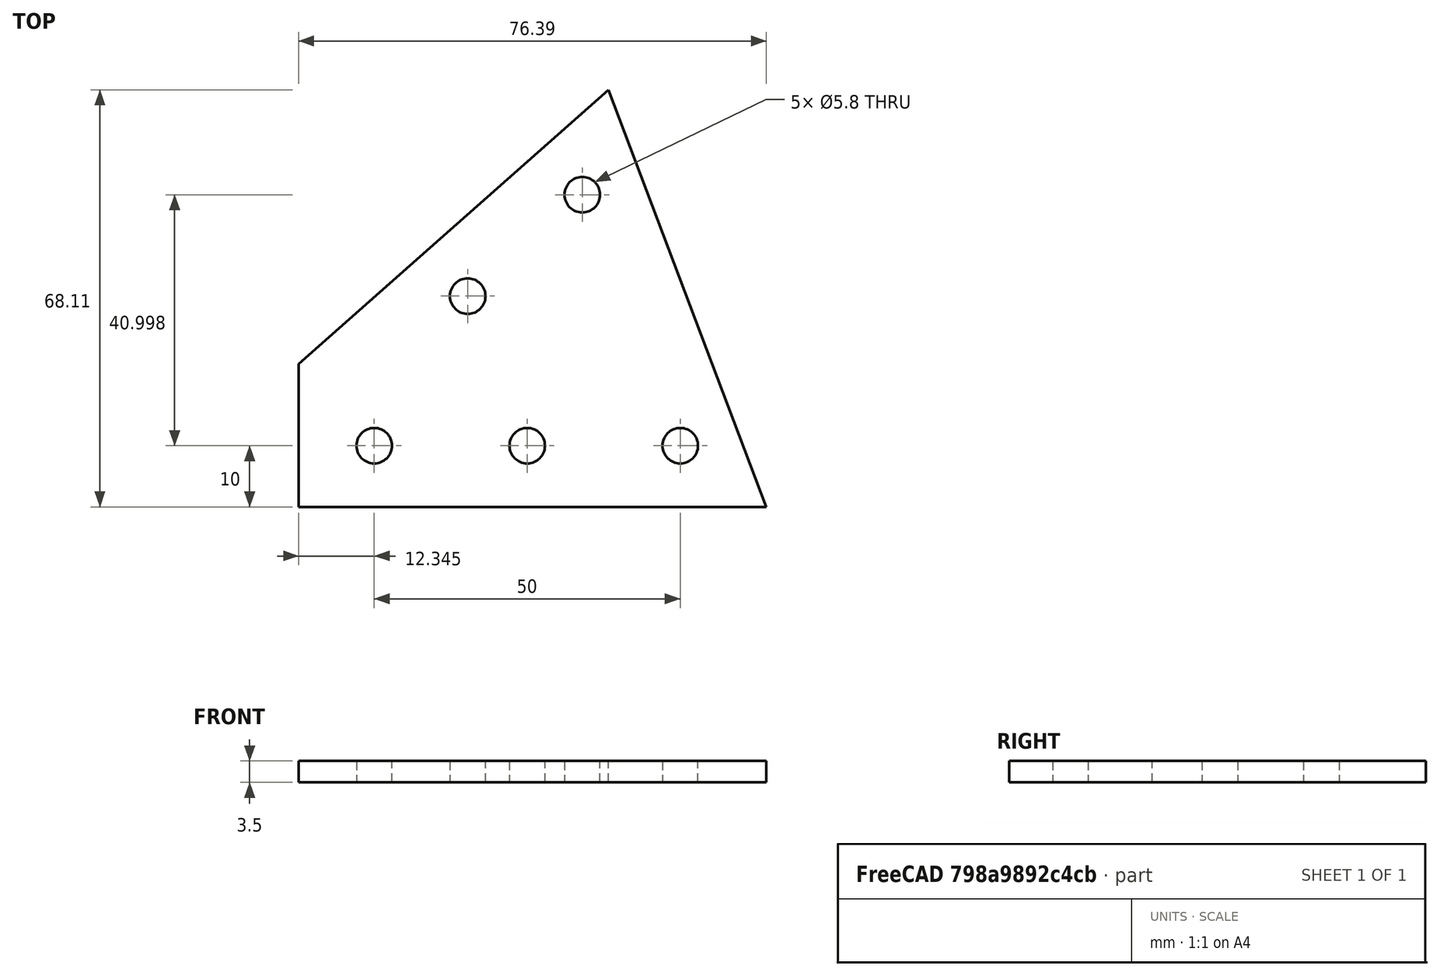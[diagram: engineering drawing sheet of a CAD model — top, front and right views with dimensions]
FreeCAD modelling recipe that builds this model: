
FCSTD DOCUMENT  (FreeCAD 0.16R6607 (Git))
Label: frame_corner_41.5_degree
License: CreativeCommons Attribution-ShareAlike
LicenseURL: http://creativecommons.org/licenses/by-sa/4.0/
objects: Sketcher::SketchObject×1, PartDesign::Pad×1
note: 3 computed .brp shape members not serialized (recipe doc carries the construction recipe); baked Part::Feature solids carry a one-line shape summary decoded from their .brp

FEATURE [Sketcher::SketchObject] Sketch
  sketch-geometry (21):
    g0: LineSegment [constr] StartX=57.2161 StartY=50.6206 StartZ=0 EndX=0 EndY=0 EndZ=0
    g1: LineSegment [constr] StartX=0 StartY=0 StartZ=0 EndX=76.3945 EndY=0 EndZ=0
    g2: LineSegment [constr] StartX=0 StartY=10 StartZ=0 EndX=76.3945 EndY=10 EndZ=0
    g3: LineSegment [constr] StartX=76.3945 StartY=10 StartZ=0 EndX=76.3945 EndY=-10 EndZ=0
    g4: LineSegment [constr] StartX=76.3945 StartY=-10 StartZ=0 EndX=0 EndY=-10 EndZ=0
    g5: LineSegment [constr] StartX=0 StartY=-10 StartZ=0 EndX=0 EndY=10 EndZ=0
    g6: LineSegment [constr] StartX=13.1421 StartY=24.9791 StartZ=0 EndX=50.5899 EndY=58.1101 EndZ=0
    g7: LineSegment [constr] StartX=50.5899 StartY=58.1101 StartZ=0 EndX=63.8423 EndY=43.131 EndZ=0
    g8: LineSegment [constr] StartX=63.8423 StartY=43.131 StartZ=0 EndX=26.3945 EndY=10 EndZ=0
    g9: LineSegment [constr] StartX=26.3945 StartY=10 StartZ=0 EndX=13.1421 EndY=24.9791 EndZ=0
    g10: LineSegment [constr] StartX=13.1421 StartY=24.9791 StartZ=0 EndX=-26.3945 EndY=-10 EndZ=0
    g11: LineSegment [constr] StartX=-26.3945 StartY=-10 StartZ=0 EndX=0 EndY=-10 EndZ=0
    g12: LineSegment StartX=0 StartY=-10 StartZ=0 EndX=0 EndY=13.3519 EndZ=0
    g13: LineSegment StartX=0 StartY=13.3519 StartZ=0 EndX=50.5899 EndY=58.1101 EndZ=0
    g14: LineSegment StartX=50.5899 StartY=58.1101 StartZ=0 EndX=76.3945 EndY=-10 EndZ=0
    g15: LineSegment StartX=76.3945 StartY=-10 StartZ=0 EndX=0 EndY=-10 EndZ=0
    g16: Circle CenterX=27.6164 CenterY=24.4329 CenterZ=0 NormalX=0 NormalY=0 NormalZ=1 Radius=2.9
    g17: Circle CenterX=46.3403 CenterY=40.9984 CenterZ=0 NormalX=0 NormalY=0 NormalZ=1 Radius=2.9
    g18: Circle CenterX=62.3447 CenterY=0 CenterZ=0 NormalX=0 NormalY=0 NormalZ=1 Radius=2.9
    g19: Circle CenterX=37.3447 CenterY=0 CenterZ=0 NormalX=0 NormalY=0 NormalZ=1 Radius=2.9
    g20: Circle CenterX=12.3447 CenterY=0 CenterZ=0 NormalX=0 NormalY=0 NormalZ=1 Radius=2.9
  constraints (58):
    c: Coincident(g0,g1)
    c: Angle(g1,g0) = 0.724312
    c: Horizontal(g1)
    c: Equal(g0,g1)
    c: Coincident(g0,g-1)
    c: Coincident(g2,g3)
    c: Coincident(g3,g4)
    c: Coincident(g4,g5)
    c: Coincident(g5,g2)
    c: Horizontal(g2)
    c: Horizontal(g4)
    c: Vertical(g3)
    c: Vertical(g5)
    c: Coincident(g6,g7)
    c: Coincident(g7,g8)
    c: Coincident(g8,g9)
    c: Coincident(g9,g6)
    c: Parallel(g6,g8)
    c: Parallel(g8,g0)
    c: Perpendicular(g8,g9)
    c: Perpendicular(g8,g7)
    c: Distance(g9) = 20
    c: DistanceY(g5) = 20
    c: PointOnObject(g0,g7)
    c: Distance(g7,g0) = 10
    c: PointOnObject(g8,g2)
    c: DistanceY(g1,g3) = -10
    c: PointOnObject(g-1,g5)
    c: PointOnObject(g1,g3)
    c: Distance(g6,g6) = 50
    c: Coincident(g10,g11)
    c: Coincident(g4,g11)
    c: Coincident(g6,g10)
    c: Angle(g11,g10) = 0.724312
    c: Horizontal(g11)
    c: Coincident(g12,g13)
    c: Coincident(g13,g14)
    c: Coincident(g14,g15)
    c: Horizontal(g15)
    c: Coincident(g4,g12)
    c: Coincident(g4,g15)
    c: PointOnObject(g12,g10)
    c: Vertical(g12)
    c: Coincident(g6,g13)
    c: Coincident(g3,g14)
    c: PointOnObject(g16,g0)
    c: PointOnObject(g20,g1)
    c: PointOnObject(g19,g1)
    c: PointOnObject(g18,g1)
    c: PointOnObject(g17,g0)
    c: Radius(g17) = 2.9
    c: Equal(g17,g16)
    c: Equal(g17,g20)
    c: Equal(g17,g19)
    c: Equal(g17,g18)
    c: Distance(g17,g16) = 25
    c: DistanceX(g19,g20) = -25
    c: DistanceX(g18,g19) = -25
FEATURE [PartDesign::Pad] Pad
  Length = 3.5
  Length2 = 100
  Sketch = -> Sketch
  Type = 0
